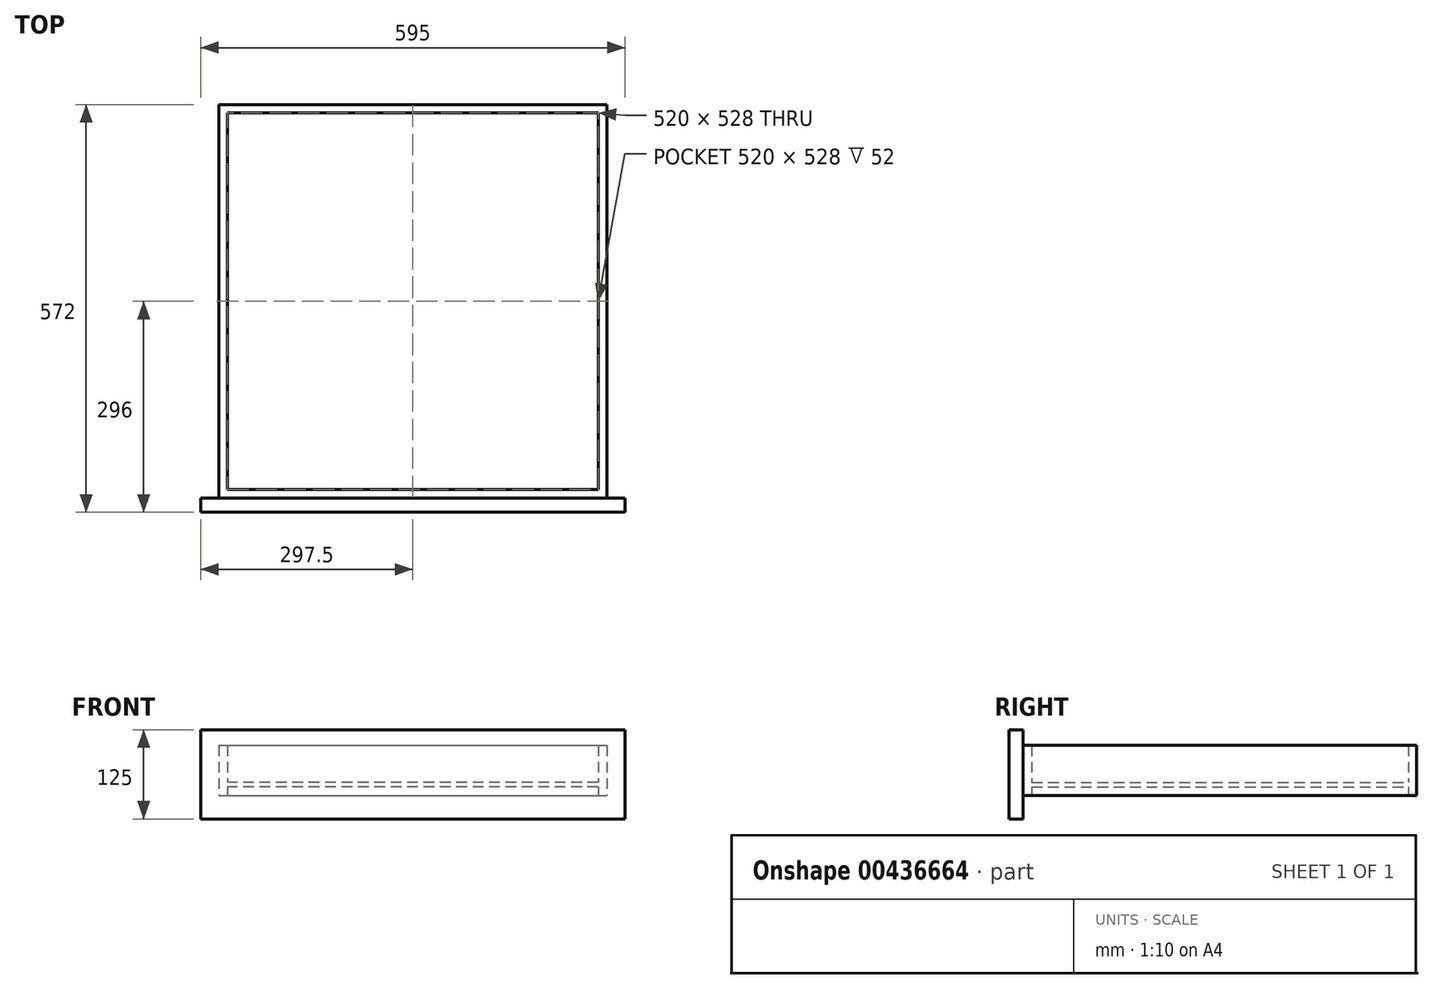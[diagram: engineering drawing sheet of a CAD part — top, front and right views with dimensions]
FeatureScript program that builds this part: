
annotation { "Feature Type Name" : "Feature", "Feature Type Description" : "" }
export const myFeature = defineFeature(function(context is Context, id is Id, definition is map)
    precondition{}
    {
        {
            var Q0;
            Q0=qCreatedBy(makeId("Front.planeOp"),FACE);
            var sketch = newSketch(context, id + "F0", { "sketchPlane" : qUnion([Q0])});
            skLineSegment(sketch, "E0.bottom", {"start": v(260, 3) * mm, "end": v(-260, 3) * mm});
            skLineSegment(sketch, "E0.top", {"start": v(260, -3) * mm, "end": v(-260, -3) * mm});
            skPoint(sketch, "E0.middle", {"position": v(0, 0) * mm});
            skLineSegment(sketch, "E1.bottom", {"start": v(-260, 55) * mm, "end": v(-272, 55) * mm});
            skLineSegment(sketch, "E1.top", {"start": v(-260, -15) * mm, "end": v(-272, -15) * mm});
            skLineSegment(sketch, "E1.left", {"start": v(-260, 55) * mm, "end": v(-260, 3) * mm});
            skLineSegment(sketch, "E1.right", {"start": v(-272, 55) * mm, "end": v(-272, -15) * mm});
            skLineSegment(sketch, "E2.bottom", {"start": v(260, 55) * mm, "end": v(272, 55) * mm});
            skLineSegment(sketch, "E2.top", {"start": v(260, -15) * mm, "end": v(272, -15) * mm});
            skLineSegment(sketch, "E2.left", {"start": v(260, 55) * mm, "end": v(260, 3) * mm});
            skLineSegment(sketch, "E2.right", {"start": v(272, 55) * mm, "end": v(272, -15) * mm});
            skLineSegment(sketch, "E3.trimOffspring", {"start": v(-260, -3) * mm, "end": v(-260, -15) * mm});
            skLineSegment(sketch, "E4.trimOffspring", {"start": v(260, -3) * mm, "end": v(260, -15) * mm});
            skSolve(sketch);
        }
        {
            var Q0;
            Q0 = qSketchRegion(id + "F0", true);
            extrude(context, id + "F1", {"entities" : qUnion([Q0]), "depth" : 552 * mm});
        }
        {
            var Q0;
            Q0=makeQuery(id+"F1.opExtrude","SWEPT_FACE",FACE,{"disambiguationData":[OSD([sQuery(id+"F0.wireOp",EDGE,"E2.left")])]});
            var sketch = newSketch(context, id + "F2", { "sketchPlane" : qUnion([Q0])});
            skLineSegment(sketch, "E5.bottom", {"start": v(0, 55) * mm, "end": v(12, 55) * mm});
            skLineSegment(sketch, "E5.top", {"start": v(0, -15) * mm, "end": v(12, -15) * mm});
            skLineSegment(sketch, "E5.left", {"start": v(0, 55) * mm, "end": v(0, -15) * mm});
            skLineSegment(sketch, "E5.right", {"start": v(12, 55) * mm, "end": v(12, -15) * mm});
            skLineSegment(sketch, "E6.bottom", {"start": v(552, 55) * mm, "end": v(540, 55) * mm});
            skLineSegment(sketch, "E6.top", {"start": v(552, -15) * mm, "end": v(540, -15) * mm});
            skLineSegment(sketch, "E6.left", {"start": v(552, 55) * mm, "end": v(552, -15) * mm});
            skLineSegment(sketch, "E6.right", {"start": v(540, 55) * mm, "end": v(540, -15) * mm});
            skSolve(sketch);
        }
        {
            var Q0;
            Q0 = qSketchRegion(id + "F2", true);
            extrude(context, id + "F3", {"entities" : qUnion([Q0]), "operationType" : NewBodyOperationType.ADD, "depth" : 520 * mm});
        }
        {
            var Q0;
            Q0=makeQuery(id+"F1.opExtrude","CAP_FACE",FACE,{"disambiguationData":[OSD([sQuery(id+"F0.wireOp",EDGE,"E0.bottom"),sQuery(id+"F0.wireOp",EDGE,"E0.top"),sQuery(id+"F0.wireOp",EDGE,"E1.bottom"),sQuery(id+"F0.wireOp",EDGE,"E1.top"),sQuery(id+"F0.wireOp",EDGE,"E1.left"),sQuery(id+"F0.wireOp",EDGE,"E1.right"),sQuery(id+"F0.wireOp",EDGE,"E2.bottom"),sQuery(id+"F0.wireOp",EDGE,"E2.top"),sQuery(id+"F0.wireOp",EDGE,"E2.left"),sQuery(id+"F0.wireOp",EDGE,"E2.right"),sQuery(id+"F0.wireOp",EDGE,"E3.trimOffspring"),sQuery(id+"F0.wireOp",EDGE,"E4.trimOffspring")])],"isStart":false});
            var sketch = newSketch(context, id + "F4", { "sketchPlane" : qUnion([Q0])});
            skLineSegment(sketch, "E7.bottom", {"start": v(-297.5, 77) * mm, "end": v(297.5, 77) * mm});
            skLineSegment(sketch, "E7.top", {"start": v(-297.5, -48) * mm, "end": v(297.5, -48) * mm});
            skLineSegment(sketch, "E7.left", {"start": v(-297.5, 77) * mm, "end": v(-297.5, -48) * mm});
            skLineSegment(sketch, "E7.right", {"start": v(297.5, 77) * mm, "end": v(297.5, -48) * mm});
            skSolve(sketch);
        }
        {
            var Q0;
            Q0 = qSketchRegion(id + "F4", true);
            extrude(context, id + "F5", {"entities" : qUnion([Q0]), "operationType" : NewBodyOperationType.ADD, "depth" : 20 * mm});
        }
    });
